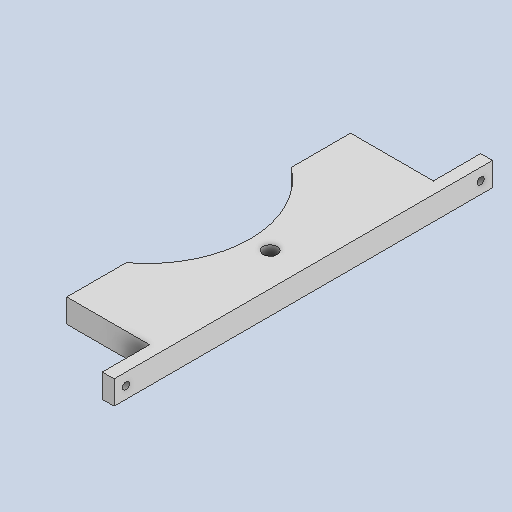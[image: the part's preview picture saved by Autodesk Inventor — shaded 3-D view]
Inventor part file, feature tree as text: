
AUTODESK INVENTOR PART (.ipt)
format: ipt  version: 2023 (Build 270158000, 158)  size: 266,752 bytes
history: native  units: mm
features: extrude x2, thread x2, sketch x2, other x1
ambient origin geometry x8: Origin, YZ Plane, XZ Plane, XY Plane, X Axis, Y Axis, Z Axis, Center Point
bodies: Body1 (feature_tree)
feature tree (7):
  other  "Твердое тело1"
  extrude  "Выдавливание1"  Depth=130.0mm
  extrude  "Выдавливание2"  Depth=120.0mm
  thread  "Резьба1"
  thread  "Резьба2"
  sketch  "Эскиз1"
  sketch  "Эскиз2"
